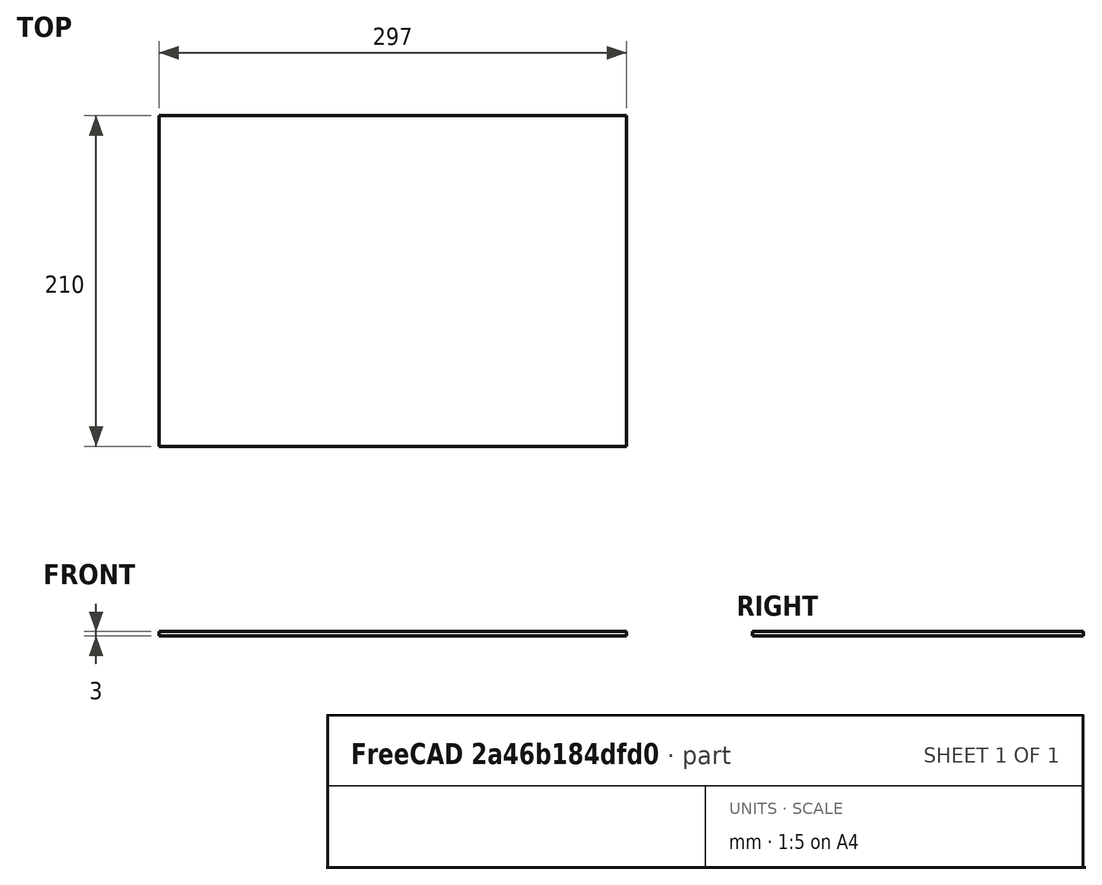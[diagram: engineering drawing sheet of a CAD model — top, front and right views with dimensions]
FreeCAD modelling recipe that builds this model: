
FCSTD DOCUMENT  (FreeCAD 0.20R29177 (Git))
Label: 1001_keyboard_Analog_paper_stencil_A4
License: All rights reserved
LicenseURL: http://en.wikipedia.org/wiki/All_rights_reserved
objects: Sketcher::SketchObject×6, PartDesign::Pad×1, PartDesign::Body×1
note: 9 computed .brp shape members not serialized (recipe doc carries the construction recipe); baked Part::Feature solids carry a one-line shape summary decoded from their .brp

FEATURE [Sketcher::SketchObject] Sketch
  FullyConstrained = true
  MapMode = 5
  Support = -> [XY_Plane]
  sketch-geometry (5):
    g0: LineSegment StartX=0 StartY=210 StartZ=0 EndX=297 EndY=210 EndZ=0
    g1: LineSegment StartX=297 StartY=210 StartZ=0 EndX=297 EndY=0 EndZ=0
    g2: LineSegment StartX=297 StartY=0 StartZ=0 EndX=0 EndY=0 EndZ=0
    g3: LineSegment StartX=0 StartY=0 StartZ=0 EndX=0 EndY=105 EndZ=0
    g4: LineSegment StartX=0 StartY=105 StartZ=0 EndX=0 EndY=210 EndZ=0
  constraints (14):
    c: Coincident(g0,g1)
    c: Coincident(g1,g2)
    c: Horizontal(g0)
    c: Horizontal(g2)
    c: Vertical(g1)
    c: DistanceY(g1,g1) = 210
    c: DistanceX(g0,g0) = 297
    c: Coincident(g3,g2)
    c: Coincident(g4,g0)
    c: Equal(g3,g4)
    c: Vertical(g4)
    c: Vertical(g3)
    c: Coincident(g3,g4)
    c: Coincident(g2,g-1)
FEATURE [PartDesign::Pad] Pad  label="A4_Landscape"
  AllowMultiFace = false
  Direction = (0,0,1)
  Length = 3
  Length2 = 100
  Profile = -> Sketch
  ReferenceAxis = -> Sketch [N_Axis]
  Type = 0
FEATURE [PartDesign::Body] Body
  Group = -> [Sketch,Pad]
  Origin = -> Origin
  Tip = -> Pad
FEATURE [Sketcher::SketchObject] Sketch002  label="ButtonsLayoutSquare"
  FullyConstrained = false
  sketch-geometry (15):
    g0: LineSegment StartX=130.72 StartY=61.5386 StartZ=0 EndX=130.72 EndY=21.5386 EndZ=0
    g1: Circle CenterX=130.72 CenterY=61.5386 CenterZ=0 NormalX=0 NormalY=0 NormalZ=1 AngleXU=0 Radius=15
    g2: Circle CenterX=130.72 CenterY=21.5386 CenterZ=0 NormalX=0 NormalY=0 NormalZ=1 AngleXU=0 Radius=15
    g3: LineSegment StartX=130.72 StartY=61.5386 StartZ=0 EndX=170.72 EndY=61.5386 EndZ=0
    g4: LineSegment StartX=130.72 StartY=21.5386 StartZ=0 EndX=170.72 EndY=21.5386 EndZ=0
    g5: LineSegment StartX=170.72 StartY=21.5386 StartZ=0 EndX=170.72 EndY=61.5386 EndZ=0
    g6: Circle CenterX=170.72 CenterY=61.5386 CenterZ=0 NormalX=0 NormalY=0 NormalZ=1 AngleXU=0 Radius=14.5
    g7: Circle CenterX=170.72 CenterY=21.5386 CenterZ=0 NormalX=0 NormalY=0 NormalZ=1 AngleXU=0 Radius=15
    g8: LineSegment StartX=130.72 StartY=21.5386 StartZ=0 EndX=150.72 EndY=41.5386 EndZ=0
    g9: LineSegment StartX=150.72 StartY=41.5386 StartZ=0 EndX=170.72 EndY=61.5386 EndZ=0
    g10: LineSegment StartX=110.72 StartY=81.5386 StartZ=0 EndX=110.72 EndY=1.53857 EndZ=0
    g11: LineSegment StartX=110.72 StartY=1.53857 StartZ=0 EndX=190.72 EndY=1.53857 EndZ=0
    g12: LineSegment StartX=190.72 StartY=1.53857 StartZ=0 EndX=190.72 EndY=81.5386 EndZ=0
    g13: LineSegment StartX=190.72 StartY=81.5386 StartZ=0 EndX=110.72 EndY=81.5386 EndZ=0
    g14: Circle CenterX=150.72 CenterY=41.5386 CenterZ=0 NormalX=0 NormalY=0 NormalZ=1 AngleXU=0 Radius=56.5685
  constraints (35):
    c: Equal(g2,g1)
    c: Coincident(g3,g1)
    c: Coincident(g4,g2)
    c: Coincident(g5,g4)
    c: Coincident(g5,g3)
    c: Equal(g3,g5)
    c: Equal(g5,g4)
    c: Coincident(g6,g3)
    c: Coincident(g7,g4)
    c: Coincident(g1,g0)
    c: Coincident(g0,g2)
    c: Angle(g0,g3) = 1.5708
    c: Distance(g6,g1) = 40
    c: Diameter(g6) = 29
    c: Vertical(g5)
    c: Vertical(g0)
    c: Coincident(g8,g2)
    c: Coincident(g9,g8)
    c: Coincident(g9,g6)
    c: Equal(g9,g8)
    c: Parallel(g9,g8)
    c: Coincident(g10,g11)
    c: Coincident(g11,g12)
    c: Coincident(g12,g13)
    c: Coincident(g13,g10)
    c: Equal(g10,g11)
    c: Equal(g10,g12)
    c: Equal(g10,g13)
    c: PointOnObject(g10,g14)
    c: PointOnObject(g11,g14)
    c: PointOnObject(g12,g14)
    c: PointOnObject(g13,g14)
    c: Coincident(g14,g8)
    c: Horizontal(g13)
    c: DistanceX(g13,g13) = 80
FEATURE [Sketcher::SketchObject] Sketch003  label="JoystickLayout4Way"
  FullyConstrained = false
  sketch-geometry (39):
    g0: LineSegment StartX=5 StartY=60 StartZ=0 EndX=100 EndY=60 EndZ=0
    g1: LineSegment StartX=100 StartY=60 StartZ=0 EndX=100 EndY=5 EndZ=0
    g2: LineSegment StartX=100 StartY=5 StartZ=0 EndX=52.5 EndY=5 EndZ=0
    g3: LineSegment StartX=52.5 StartY=5 StartZ=0 EndX=5 EndY=5 EndZ=0
    g4: LineSegment StartX=5 StartY=5 StartZ=0 EndX=5 EndY=32.5 EndZ=0
    g5: LineSegment StartX=5 StartY=32.5 StartZ=0 EndX=5 EndY=60 EndZ=0
    g6: LineSegment StartX=5 StartY=32.5 StartZ=0 EndX=52.5 EndY=32.5 EndZ=0
    g7: Circle CenterX=52.5 CenterY=32.5 CenterZ=0 NormalX=0 NormalY=0 NormalZ=1 AngleXU=0 Radius=15
    g8: LineSegment StartX=52.5 StartY=32.5 StartZ=0 EndX=100 EndY=32.5 EndZ=0
    g9: ArcOfCircle CenterX=10.5 CenterY=52.5 CenterZ=0 NormalX=0 NormalY=0 NormalZ=1 AngleXU=0 Radius=2.6 StartAngle=1.5708 EndAngle=4.71239
    g10: ArcOfCircle CenterX=13.1 CenterY=52.5 CenterZ=0 NormalX=0 NormalY=0 NormalZ=1 AngleXU=0 Radius=2.6 StartAngle=4.71239 EndAngle=7.85398
    g11: LineSegment StartX=10.5 StartY=49.9 StartZ=0 EndX=13.1 EndY=49.9 EndZ=0
    g12: LineSegment StartX=13.1 StartY=55.1 StartZ=0 EndX=10.5 EndY=55.1 EndZ=0
    g13: LineSegment StartX=10.5 StartY=55.1 StartZ=0 EndX=7.9 EndY=55.1 EndZ=0
    g14: LineSegment StartX=13.1 StartY=55.1 StartZ=0 EndX=15.7 EndY=55.1 EndZ=0
    g15: ArcOfCircle CenterX=94.5 CenterY=52.5 CenterZ=0 NormalX=0 NormalY=0 NormalZ=1 AngleXU=0 Radius=2.6 StartAngle=4.71239 EndAngle=7.85398
    g16: LineSegment StartX=94.5 StartY=55.1 StartZ=0 EndX=91.9 EndY=55.1 EndZ=0
    g17: LineSegment StartX=91.9 StartY=49.9 StartZ=0 EndX=94.5 EndY=49.9 EndZ=0
    g18: ArcOfCircle CenterX=91.9 CenterY=52.5 CenterZ=0 NormalX=0 NormalY=0 NormalZ=1 AngleXU=0 Radius=2.6 StartAngle=1.5708 EndAngle=4.71239
    g19: LineSegment StartX=10.5 StartY=9.9 StartZ=0 EndX=13.1 EndY=9.9 EndZ=0
    g20: ArcOfCircle CenterX=13.1 CenterY=12.5 CenterZ=0 NormalX=0 NormalY=0 NormalZ=1 AngleXU=0 Radius=2.6 StartAngle=4.71239 EndAngle=7.85398
    g21: LineSegment StartX=13.1 StartY=15.1 StartZ=0 EndX=10.5 EndY=15.1 EndZ=0
    g22: ArcOfCircle CenterX=10.5 CenterY=12.5 CenterZ=0 NormalX=0 NormalY=0 NormalZ=1 AngleXU=0 Radius=2.6 StartAngle=1.5708 EndAngle=4.71239
    g23: ArcOfCircle CenterX=91.9 CenterY=12.5 CenterZ=0 NormalX=0 NormalY=0 NormalZ=1 AngleXU=0 Radius=2.6 StartAngle=1.5708 EndAngle=4.71239
    g24: LineSegment StartX=91.9 StartY=9.9 StartZ=0 EndX=94.5 EndY=9.9 EndZ=0
    g25: LineSegment StartX=94.5 StartY=15.1 StartZ=0 EndX=91.9 EndY=15.1 EndZ=0
    g26: ArcOfCircle CenterX=94.5 CenterY=12.5 CenterZ=0 NormalX=0 NormalY=0 NormalZ=1 AngleXU=0 Radius=2.6 StartAngle=4.71239 EndAngle=7.85398
    g27: LineSegment StartX=52.5 StartY=5 StartZ=0 EndX=52.5 EndY=7.9007 EndZ=0
    g28: LineSegment StartX=5 StartY=32.5 StartZ=0 EndX=7.9007 EndY=32.5 EndZ=0
    g29: LineSegment StartX=100 StartY=32.5 StartZ=0 EndX=97.0993 EndY=32.5 EndZ=0
    g30: LineSegment StartX=52.5 StartY=60 StartZ=0 EndX=52.5 EndY=57.0993 EndZ=0
    g31: LineSegment StartX=100 StartY=60 StartZ=0 EndX=43 EndY=60 EndZ=0
    g32: LineSegment StartX=43 StartY=60 StartZ=0 EndX=43 EndY=70 EndZ=0
    g33: LineSegment StartX=23 StartY=70 StartZ=0 EndX=23 EndY=60 EndZ=0
    g34: LineSegment StartX=23 StartY=60 StartZ=0 EndX=5 EndY=60 EndZ=0
    g35: LineSegment StartX=23 StartY=70 StartZ=0 EndX=33 EndY=70 EndZ=0
    g36: LineSegment StartX=33 StartY=70 StartZ=0 EndX=43 EndY=70 EndZ=0
    g37: LineSegment StartX=10.5 StartY=49.9 StartZ=0 EndX=10.5 EndY=32.5 EndZ=0
    g38: LineSegment StartX=10.5 StartY=32.5 StartZ=0 EndX=10.5 EndY=15.1 EndZ=0
  constraints (107):
    c: Coincident(g0,g1)
    c: Coincident(g1,g2)
    c: Horizontal(g0)
    c: Horizontal(g2)
    c: Vertical(g1)
    c: DistanceY(g1,g1) = 55
    c: DistanceX(g0,g0) = 95
    c: Coincident(g3,g2)
    c: Coincident(g4,g3)
    c: Coincident(g5,g4)
    c: Coincident(g5,g0)
    c: Vertical(g5)
    c: Vertical(g4)
    c: Horizontal(g3)
    c: Equal(g3,g2)
    c: Equal(g4,g5)
    c: Coincident(g6,g4)
    c: Horizontal(g6)
    c: Coincident(g7,g6)
    c: Coincident(g8,g6)
    c: PointOnObject(g8,g1)
    c: Horizontal(g8)
    c: Equal(g8,g6)
    c: Diameter(g7) = 30
    c: Tangent(g9,g11) = -1.5708
    c: Tangent(g11,g10) = -1.5708
    c: Tangent(g10,g12) = -1.5708
    c: Tangent(g12,g9) = -1.5708
    c: Equal(g9,g10)
    c: Horizontal(g11)
    c: DistanceY(g10,g10) = 5.2
    c: Coincident(g13,g9)
    c: Horizontal(g13)
    c: Coincident(g14,g10)
    c: Horizontal(g14)
    c: Equal(g14,g13)
    c: DistanceX(g13,g13) = 2.6
    c: DistanceX(g13,g14) = 7.8
    c: Tangent(g18,g17) = -1.5708
    c: Tangent(g17,g15) = -1.5708
    c: Tangent(g15,g16) = -1.5708
    c: Tangent(g16,g18) = -1.5708
    c: Equal(g18,g15)
    c: Horizontal(g17)
    c: Equal(g10,g15) = 5.2
    c: Tangent(g22,g19) = -1.5708
    c: Tangent(g19,g20) = -1.5708
    c: Tangent(g20,g21) = -1.5708
    c: Tangent(g21,g22) = -1.5708
    c: Equal(g22,g20)
    c: Horizontal(g19)
    c: Equal(g10,g20) = 5.2
    c: Tangent(g23,g24) = -1.5708
    c: Tangent(g24,g26) = -1.5708
    c: Tangent(g26,g25) = -1.5708
    c: Tangent(g25,g23) = -1.5708
    c: Equal(g23,g26)
    c: Horizontal(g24)
    c: Equal(g10,g26) = 5.2
    c: Equal(g21,g16)
    c: Equal(g16,g25)
    c: Equal(g25,g11)
    c: Vertical(g21,g9)
    c: DistanceX(g9,g6) = 42
    c: Horizontal(g23,g20)
    c: Vertical(g23,g17)
    c: DistanceX(g9,g15) = 84
    c: Horizontal(g10,g16)
    c: Coincident(g27,g2)
    c: Vertical(g27)
    c: Coincident(g28,g4)
    c: PointOnObject(g28,g6)
    c: Equal(g28,g27)
    c: Coincident(g29,g8)
    c: PointOnObject(g29,g8)
    c: Equal(g29,g27)
    c: PointOnObject(g30,g0)
    c: Vertical(g30)
    c: Equal(g30,g29)
    c: Vertical(g30,g27)
    c: Coincident(g31,g1)
    c: PointOnObject(g31,g0)
    c: Coincident(g32,g31)
    c: Vertical(g32)
    c: PointOnObject(g33,g0)
    c: Vertical(g33)
    c: Coincident(g34,g33)
    c: Coincident(g34,g5)
    c: DistanceX(g33,g32) = 20
    c: DistanceY(g33,g33) = 10
    c: Coincident(g35,g33)
    c: Horizontal(g35)
    c: Coincident(g36,g35)
    c: Coincident(g36,g32)
    c: Horizontal(g36)
    c: Equal(g36,g35)
    c: DistanceX(g5,g35) = 28
    c: Coincident(g37,g9)
    c: PointOnObject(g37,g6)
    c: Vertical(g37)
    c: Coincident(g38,g37)
    c: Coincident(g38,g21)
    c: Equal(g38,g37)
    c: DistanceY(g22,g9) = 40
    c: DistanceX(g-1,g3) = 5
    c: DistanceY(g-1,g3) = 5
    c: DistanceX(g7,g15) = 42
FEATURE [Sketcher::SketchObject] Sketch007  label="JoystickAnalog"
  FullyConstrained = false
  MapMode = 5
  Support = -> [XY_Plane]
  sketch-geometry (90):
    g0: Circle CenterX=243.856 CenterY=93.0122 CenterZ=0 NormalX=0 NormalY=0 NormalZ=1 AngleXU=0 Radius=20
    g1: LineSegment StartX=243.856 StartY=93.0122 StartZ=0 EndX=201.356 EndY=93.0122 EndZ=0
    g2: LineSegment StartX=243.856 StartY=93.0122 StartZ=0 EndX=286.356 EndY=93.0122 EndZ=0
    g3: LineSegment StartX=201.356 StartY=93.0122 StartZ=0 EndX=201.356 EndY=113.012 EndZ=0
    g4: LineSegment StartX=201.356 StartY=93.0122 StartZ=0 EndX=201.356 EndY=73.0122 EndZ=0
    g5: LineSegment StartX=286.356 StartY=93.0122 StartZ=0 EndX=286.356 EndY=73.0122 EndZ=0
    g6: LineSegment StartX=286.356 StartY=93.0122 StartZ=0 EndX=286.356 EndY=113.012 EndZ=0
    g7: LineSegment StartX=243.856 StartY=93.0122 StartZ=0 EndX=243.856 EndY=123.012 EndZ=0
    g8: LineSegment StartX=243.856 StartY=93.0122 StartZ=0 EndX=243.856 EndY=63.0122 EndZ=0
    g9: LineSegment StartX=243.856 StartY=123.012 StartZ=0 EndX=196.356 EndY=123.012 EndZ=0
    g10: LineSegment StartX=243.856 StartY=123.012 StartZ=0 EndX=291.356 EndY=123.012 EndZ=0
    g11: LineSegment StartX=243.856 StartY=63.0122 StartZ=0 EndX=196.356 EndY=63.0122 EndZ=0
    g12: LineSegment StartX=196.356 StartY=63.0122 StartZ=0 EndX=196.356 EndY=123.012 EndZ=0
    g13: LineSegment StartX=243.856 StartY=63.0122 StartZ=0 EndX=291.356 EndY=63.0122 EndZ=0
    g14: LineSegment StartX=291.356 StartY=63.0122 StartZ=0 EndX=291.356 EndY=123.012 EndZ=0
    g15: ArcOfCircle CenterX=201.356 CenterY=113.012 CenterZ=0 NormalX=0 NormalY=0 NormalZ=1 AngleXU=0 Radius=2.5 StartAngle=1.5708 EndAngle=4.71239
    g16: ArcOfCircle CenterX=206.356 CenterY=113.012 CenterZ=0 NormalX=0 NormalY=0 NormalZ=1 AngleXU=0 Radius=2.5 StartAngle=4.71239 EndAngle=7.85398
    g17: LineSegment StartX=201.356 StartY=110.512 StartZ=0 EndX=206.356 EndY=110.512 EndZ=0
    g18: LineSegment StartX=206.356 StartY=115.512 StartZ=0 EndX=201.356 EndY=115.512 EndZ=0
    g19: ArcOfCircle CenterX=201.356 CenterY=73.0122 CenterZ=0 NormalX=0 NormalY=0 NormalZ=1 AngleXU=0 Radius=2.5 StartAngle=1.5708 EndAngle=4.71239
    g20: ArcOfCircle CenterX=206.356 CenterY=73.0122 CenterZ=0 NormalX=0 NormalY=0 NormalZ=1 AngleXU=0 Radius=2.5 StartAngle=4.71239 EndAngle=7.85398
    g21: LineSegment StartX=201.356 StartY=70.5122 StartZ=0 EndX=206.356 EndY=70.5122 EndZ=0
    g22: LineSegment StartX=206.356 StartY=75.5122 StartZ=0 EndX=201.356 EndY=75.5122 EndZ=0
    g23: ArcOfCircle CenterX=286.356 CenterY=73.0122 CenterZ=0 NormalX=0 NormalY=0 NormalZ=1 AngleXU=0 Radius=2.5 StartAngle=4.71239 EndAngle=7.85398
    g24: ArcOfCircle CenterX=281.356 CenterY=73.0122 CenterZ=0 NormalX=0 NormalY=0 NormalZ=1 AngleXU=0 Radius=2.5 StartAngle=1.5708 EndAngle=4.71239
    g25: LineSegment StartX=286.356 StartY=75.5122 StartZ=0 EndX=281.356 EndY=75.5122 EndZ=0
    g26: LineSegment StartX=281.356 StartY=70.5122 StartZ=0 EndX=286.356 EndY=70.5122 EndZ=0
    g27: ArcOfCircle CenterX=286.356 CenterY=113.012 CenterZ=0 NormalX=0 NormalY=0 NormalZ=1 AngleXU=0 Radius=2.5 StartAngle=4.71239 EndAngle=7.85398
    g28: ArcOfCircle CenterX=281.356 CenterY=113.012 CenterZ=0 NormalX=0 NormalY=0 NormalZ=1 AngleXU=0 Radius=2.5 StartAngle=1.5708 EndAngle=4.71239
    g29: LineSegment StartX=286.356 StartY=115.512 StartZ=0 EndX=281.356 EndY=115.512 EndZ=0
    g30: LineSegment StartX=281.356 StartY=110.512 StartZ=0 EndX=286.356 EndY=110.512 EndZ=0
    g31: LineSegment StartX=201.356 StartY=93.0122 StartZ=0 EndX=196.356 EndY=93.0122 EndZ=0
    g32: LineSegment StartX=286.356 StartY=93.0122 StartZ=0 EndX=291.356 EndY=93.0122 EndZ=0
    g33: LineSegment StartX=243.856 StartY=123.012 StartZ=0 EndX=243.856 EndY=118.012 EndZ=0
    g34: LineSegment StartX=196.356 StartY=63.0122 StartZ=0 EndX=236.356 EndY=63.0122 EndZ=0
    g35: LineSegment StartX=236.356 StartY=63.0122 StartZ=0 EndX=236.356 EndY=51.0122 EndZ=0
    g36: LineSegment StartX=236.356 StartY=51.0122 StartZ=0 EndX=251.356 EndY=51.0122 EndZ=0
    g37: LineSegment StartX=251.356 StartY=51.0122 StartZ=0 EndX=251.356 EndY=63.0122 EndZ=0
    g38: LineSegment StartX=251.356 StartY=63.0122 StartZ=0 EndX=291.356 EndY=63.0122 EndZ=0
    g39: LineSegment StartX=196.356 StartY=123.012 StartZ=0 EndX=228.856 EndY=123.012 EndZ=0
    g40: LineSegment StartX=228.856 StartY=123.012 StartZ=0 EndX=228.856 EndY=127.012 EndZ=0
    g41: LineSegment StartX=233.856 StartY=127.012 StartZ=0 EndX=233.856 EndY=123.012 EndZ=0
    g42: LineSegment StartX=233.856 StartY=123.012 StartZ=0 EndX=243.856 EndY=123.012 EndZ=0
    g43: LineSegment StartX=228.856 StartY=127.012 StartZ=0 EndX=231.356 EndY=127.012 EndZ=0
    g44: LineSegment StartX=231.356 StartY=127.012 StartZ=0 EndX=233.856 EndY=127.012 EndZ=0
    g45: Circle CenterX=242.711 CenterY=174.033 CenterZ=0 NormalX=0 NormalY=0 NormalZ=1 AngleXU=0 Radius=20
    g46: LineSegment StartX=242.711 StartY=174.033 StartZ=0 EndX=200.211 EndY=174.033 EndZ=0
    g47: LineSegment StartX=242.711 StartY=174.033 StartZ=0 EndX=285.211 EndY=174.033 EndZ=0
    g48: LineSegment StartX=200.211 StartY=174.033 StartZ=0 EndX=200.211 EndY=194.033 EndZ=0
    g49: LineSegment StartX=200.211 StartY=174.033 StartZ=0 EndX=200.211 EndY=154.033 EndZ=0
    g50: LineSegment StartX=285.211 StartY=174.033 StartZ=0 EndX=285.211 EndY=154.033 EndZ=0
    g51: LineSegment StartX=285.211 StartY=174.033 StartZ=0 EndX=285.211 EndY=194.033 EndZ=0
    g52: LineSegment StartX=242.711 StartY=174.033 StartZ=0 EndX=242.711 EndY=204.033 EndZ=0
    g53: LineSegment StartX=242.711 StartY=174.033 StartZ=0 EndX=242.711 EndY=144.033 EndZ=0
    g54: LineSegment StartX=242.711 StartY=204.033 StartZ=0 EndX=195.211 EndY=204.033 EndZ=0
    g55: LineSegment StartX=242.711 StartY=204.033 StartZ=0 EndX=290.211 EndY=204.033 EndZ=0
    g56: LineSegment StartX=242.711 StartY=144.033 StartZ=0 EndX=195.211 EndY=144.033 EndZ=0
    g57: LineSegment StartX=195.211 StartY=144.033 StartZ=0 EndX=195.211 EndY=204.033 EndZ=0
    g58: LineSegment StartX=242.711 StartY=144.033 StartZ=0 EndX=290.211 EndY=144.033 EndZ=0
    g59: LineSegment StartX=290.211 StartY=144.033 StartZ=0 EndX=290.211 EndY=204.033 EndZ=0
    g60: ArcOfCircle CenterX=200.211 CenterY=194.033 CenterZ=0 NormalX=0 NormalY=0 NormalZ=1 AngleXU=0 Radius=2.5 StartAngle=1.5708 EndAngle=4.71239
    g61: ArcOfCircle CenterX=205.211 CenterY=194.033 CenterZ=0 NormalX=0 NormalY=0 NormalZ=1 AngleXU=0 Radius=2.5 StartAngle=4.71239 EndAngle=7.85398
    g62: LineSegment StartX=200.211 StartY=191.533 StartZ=0 EndX=205.211 EndY=191.533 EndZ=0
    g63: LineSegment StartX=205.211 StartY=196.533 StartZ=0 EndX=200.211 EndY=196.533 EndZ=0
    g64: ArcOfCircle CenterX=200.211 CenterY=154.033 CenterZ=0 NormalX=0 NormalY=0 NormalZ=1 AngleXU=0 Radius=2.5 StartAngle=1.5708 EndAngle=4.71239
    g65: ArcOfCircle CenterX=205.211 CenterY=154.033 CenterZ=0 NormalX=0 NormalY=0 NormalZ=1 AngleXU=0 Radius=2.5 StartAngle=4.71239 EndAngle=7.85398
    g66: LineSegment StartX=200.211 StartY=151.533 StartZ=0 EndX=205.211 EndY=151.533 EndZ=0
    g67: LineSegment StartX=205.211 StartY=156.533 StartZ=0 EndX=200.211 EndY=156.533 EndZ=0
    g68: ArcOfCircle CenterX=285.211 CenterY=154.033 CenterZ=0 NormalX=0 NormalY=0 NormalZ=1 AngleXU=0 Radius=2.5 StartAngle=4.71239 EndAngle=7.85398
    g69: ArcOfCircle CenterX=280.211 CenterY=154.033 CenterZ=0 NormalX=0 NormalY=0 NormalZ=1 AngleXU=0 Radius=2.5 StartAngle=1.5708 EndAngle=4.71239
    g70: LineSegment StartX=285.211 StartY=156.533 StartZ=0 EndX=280.211 EndY=156.533 EndZ=0
    g71: LineSegment StartX=280.211 StartY=151.533 StartZ=0 EndX=285.211 EndY=151.533 EndZ=0
    g72: ArcOfCircle CenterX=285.211 CenterY=194.033 CenterZ=0 NormalX=0 NormalY=0 NormalZ=1 AngleXU=0 Radius=2.5 StartAngle=4.71239 EndAngle=7.85398
    g73: ArcOfCircle CenterX=280.211 CenterY=194.033 CenterZ=0 NormalX=0 NormalY=0 NormalZ=1 AngleXU=0 Radius=2.5 StartAngle=1.5708 EndAngle=4.71239
    g74: LineSegment StartX=285.211 StartY=196.533 StartZ=0 EndX=280.211 EndY=196.533 EndZ=0
    g75: LineSegment StartX=280.211 StartY=191.533 StartZ=0 EndX=285.211 EndY=191.533 EndZ=0
    g76: LineSegment StartX=200.211 StartY=174.033 StartZ=0 EndX=195.211 EndY=174.033 EndZ=0
    g77: LineSegment StartX=285.211 StartY=174.033 StartZ=0 EndX=290.211 EndY=174.033 EndZ=0
    g78: LineSegment StartX=242.711 StartY=204.033 StartZ=0 EndX=242.711 EndY=199.033 EndZ=0
    g79: LineSegment StartX=195.211 StartY=144.033 StartZ=0 EndX=235.211 EndY=144.033 EndZ=0
    g80: LineSegment StartX=235.211 StartY=144.033 StartZ=0 EndX=235.211 EndY=132.033 EndZ=0
    g81: LineSegment StartX=235.211 StartY=132.033 StartZ=0 EndX=250.211 EndY=132.033 EndZ=0
    g82: LineSegment StartX=250.211 StartY=132.033 StartZ=0 EndX=250.211 EndY=144.033 EndZ=0
    g83: LineSegment StartX=250.211 StartY=144.033 StartZ=0 EndX=290.211 EndY=144.033 EndZ=0
    g84: LineSegment StartX=195.211 StartY=204.033 StartZ=0 EndX=227.711 EndY=204.033 EndZ=0
    g85: LineSegment StartX=227.711 StartY=204.033 StartZ=0 EndX=227.711 EndY=208.033 EndZ=0
    g86: LineSegment StartX=232.711 StartY=208.033 StartZ=0 EndX=232.711 EndY=204.033 EndZ=0
    g87: LineSegment StartX=232.711 StartY=204.033 StartZ=0 EndX=242.711 EndY=204.033 EndZ=0
    g88: LineSegment StartX=227.711 StartY=208.033 StartZ=0 EndX=230.211 EndY=208.033 EndZ=0
    g89: LineSegment StartX=230.211 StartY=208.033 StartZ=0 EndX=232.711 EndY=208.033 EndZ=0
  constraints (234):
    c: Diameter(g0) = 40
    c: Coincident(g1,g0)
    c: Horizontal(g1)
    c: Coincident(g2,g0)
    c: Horizontal(g2)
    c: Coincident(g3,g1)
    c: Vertical(g3)
    c: Coincident(g4,g1)
    c: Vertical(g4)
    c: Coincident(g5,g2)
    c: Vertical(g5)
    c: Coincident(g6,g2)
    c: Vertical(g6)
    c: Equal(g4,g3)
    c: Equal(g3,g5)
    c: Equal(g5,g6)
    c: Equal(g2,g1)
    c: Coincident(g7,g0)
    c: Vertical(g7)
    c: Coincident(g8,g0)
    c: Vertical(g8)
    c: Equal(g8,g7)
    c: DistanceY(g4,g3) = 40
    c: DistanceX(g3,g6) = 85
    c: DistanceY(g8,g7) = 60
    c: Coincident(g9,g7)
    c: Coincident(g10,g9)
    c: Equal(g10,g9)
    c: Horizontal(g9)
    c: Horizontal(g10)
    c: DistanceX(g9,g10) = 95
    c: Coincident(g11,g8)
    c: Horizontal(g11)
    c: Coincident(g12,g9)
    c: Vertical(g12)
    c: Coincident(g13,g11)
    c: Coincident(g14,g13)
    c: Coincident(g14,g10)
    c: Horizontal(g13)
    c: Vertical(g14)
    c: Coincident(g11,g12)
    c: Tangent(g15,g17) = -1.5708
    c: Tangent(g17,g16) = -1.5708
    c: Tangent(g16,g18) = -1.5708
    c: Tangent(g18,g15) = -1.5708
    c: Equal(g15,g16)
    c: Coincident(g15,g3)
    c: Horizontal(g17)
    c: Tangent(g19,g21) = -1.5708
    c: Tangent(g21,g20) = -1.5708
    c: Tangent(g20,g22) = -1.5708
    c: Tangent(g22,g19) = -1.5708
    c: Equal(g19,g20)
    c: Coincident(g19,g4)
    c: Horizontal(g21)
    c: Tangent(g23,g25) = -1.5708
    c: Tangent(g25,g24) = -1.5708
    c: Tangent(g24,g26) = -1.5708
    c: Tangent(g26,g23) = -1.5708
    c: Equal(g23,g24)
    c: Coincident(g23,g5)
    c: Horizontal(g25)
    c: Tangent(g27,g29) = -1.5708
    c: Tangent(g29,g28) = -1.5708
    c: Tangent(g28,g30) = -1.5708
    c: Tangent(g30,g27) = -1.5708
    c: Equal(g27,g28)
    c: Coincident(g27,g6)
    c: Horizontal(g29)
    c: Equal(g18,g22)
    c: Equal(g22,g25)
    c: Equal(g25,g29)
    c: Equal(g20,g24)
    c: Equal(g24,g28)
    c: Equal(g28,g16)
    c: Diameter(g16) = 5
    c: DistanceX(g18,g18) = 5
    c: Coincident(g31,g1)
    c: PointOnObject(g31,g12)
    c: Horizontal(g31)
    c: Coincident(g32,g2)
    c: PointOnObject(g32,g14)
    c: Horizontal(g32)
    c: Coincident(g33,g9)
    c: PointOnObject(g33,g7)
    c: Equal(g33,g32)
    c: Coincident(g34,g12)
    c: PointOnObject(g34,g11)
    c: Coincident(g35,g34)
    c: Vertical(g35)
    c: Coincident(g36,g35)
    c: Horizontal(g36)
    c: Coincident(g37,g36)
    c: PointOnObject(g37,g13)
    c: Coincident(g38,g37)
    c: Coincident(g38,g14)
    c: Equal(g38,g34)
    c: DistanceX(g36,g36) = 15
    c: DistanceY(g35,g35) = 12
    c: Coincident(g39,g12)
    c: PointOnObject(g39,g9)
    c: Coincident(g40,g39)
    c: PointOnObject(g41,g9)
    c: Coincident(g42,g41)
    c: Coincident(g42,g10)
    c: Vertical(g40)
    c: Vertical(g41)
    c: Coincident(g43,g40)
    c: Horizontal(g43)
    c: Coincident(g44,g43)
    c: Coincident(g44,g41)
    c: Horizontal(g44)
    c: Equal(g44,g43)
    c: DistanceX(g12,g43) = 35
    c: DistanceX(g40,g41) = 5
    c: DistanceY(g40,g40) = 4
    c: Vertical(g37)
    c: Equal(g0,g45) = 40
    c: Coincident(g46,g45)
    c: Horizontal(g46)
    c: Coincident(g47,g45)
    c: Horizontal(g47)
    c: Coincident(g48,g46)
    c: Vertical(g48)
    c: Coincident(g49,g46)
    c: Vertical(g49)
    c: Coincident(g50,g47)
    c: Vertical(g50)
    c: Coincident(g51,g47)
    c: Vertical(g51)
    c: Equal(g49,g48)
    c: Equal(g48,g50)
    c: Equal(g50,g51)
    c: Equal(g47,g46)
    c: Coincident(g52,g45)
    c: Vertical(g52)
    c: Coincident(g53,g45)
    c: Vertical(g53)
    c: Equal(g53,g52)
    c: DistanceY(g49,g48) = 40
    c: DistanceX(g48,g51) = 85
    c: DistanceY(g53,g52) = 60
    c: Coincident(g54,g52)
    c: Coincident(g55,g54)
    c: Equal(g55,g54)
    c: Horizontal(g54)
    c: Horizontal(g55)
    c: DistanceX(g54,g55) = 95
    c: Coincident(g56,g53)
    c: Horizontal(g56)
    c: Coincident(g57,g54)
    c: Vertical(g57)
    c: Coincident(g58,g56)
    c: Coincident(g59,g58)
    c: Coincident(g59,g55)
    c: Horizontal(g58)
    c: Vertical(g59)
    c: Coincident(g56,g57)
    c: Tangent(g60,g62) = -1.5708
    c: Tangent(g62,g61) = -1.5708
    c: Tangent(g61,g63) = -1.5708
    c: Tangent(g63,g60) = -1.5708
    c: Equal(g60,g61)
    c: Coincident(g60,g48)
    c: Horizontal(g62)
    c: Tangent(g64,g66) = -1.5708
    c: Tangent(g66,g65) = -1.5708
    c: Tangent(g65,g67) = -1.5708
    c: Tangent(g67,g64) = -1.5708
    c: Equal(g64,g65)
    c: Coincident(g64,g49)
    c: Horizontal(g66)
    c: Tangent(g68,g70) = -1.5708
    c: Tangent(g70,g69) = -1.5708
    c: Tangent(g69,g71) = -1.5708
    c: Tangent(g71,g68) = -1.5708
    c: Equal(g68,g69)
    c: Coincident(g68,g50)
    c: Horizontal(g70)
    c: Tangent(g72,g74) = -1.5708
    c: Tangent(g74,g73) = -1.5708
    c: Tangent(g73,g75) = -1.5708
    c: Tangent(g75,g72) = -1.5708
    c: Equal(g72,g73)
    c: Coincident(g72,g51)
    c: Horizontal(g74)
    c: Equal(g63,g67)
    c: Equal(g67,g70)
    c: Equal(g70,g74)
    c: Equal(g65,g69)
    c: Equal(g69,g73)
    c: Equal(g73,g61)
    c: Equal(g16,g61) = 5
    c: Equal(g18,g63) = 5
    c: Coincident(g76,g46)
    c: PointOnObject(g76,g57)
    c: Horizontal(g76)
    c: Coincident(g77,g47)
    c: PointOnObject(g77,g59)
    c: Horizontal(g77)
    c: Coincident(g78,g54)
    c: PointOnObject(g78,g52)
    c: Equal(g78,g77)
    c: Coincident(g79,g57)
    c: PointOnObject(g79,g56)
    c: Coincident(g80,g79)
    c: Vertical(g80)
    c: Coincident(g81,g80)
    c: Horizontal(g81)
    c: Coincident(g82,g81)
    c: PointOnObject(g82,g58)
    c: Coincident(g83,g82)
    c: Coincident(g83,g59)
    c: Equal(g83,g79)
    c: Equal(g36,g81) = 15
    c: Equal(g35,g80) = 12
    c: Coincident(g84,g57)
    c: PointOnObject(g84,g54)
    c: Coincident(g85,g84)
    c: PointOnObject(g86,g54)
    c: Coincident(g87,g86)
    c: Coincident(g87,g55)
    c: Vertical(g85)
    c: Vertical(g86)
    c: Coincident(g88,g85)
    c: Horizontal(g88)
    c: Coincident(g89,g88)
    c: Coincident(g89,g86)
    c: Horizontal(g89)
    c: Equal(g89,g88)
    c: DistanceX(g57,g88) = 35
    c: DistanceX(g85,g86) = 5
    c: Equal(g40,g85) = 4
    c: Vertical(g82)
FEATURE [Sketcher::SketchObject] Sketch008  label="ButtonsLayoutLTLS"
  FullyConstrained = false
  sketch-geometry (20):
    g0: Circle CenterX=26.5961 CenterY=184.248 CenterZ=0 NormalX=0 NormalY=0 NormalZ=1 AngleXU=0 Radius=15
    g1: Circle CenterX=66.5961 CenterY=184.248 CenterZ=0 NormalX=0 NormalY=0 NormalZ=1 AngleXU=0 Radius=14.5
    g2: LineSegment StartX=86.5961 StartY=204.248 StartZ=0 EndX=6.59611 EndY=204.248 EndZ=0
    g3: LineSegment StartX=46.5961 StartY=164.248 StartZ=0 EndX=6.59611 EndY=164.248 EndZ=0
    g4: LineSegment StartX=46.5961 StartY=164.248 StartZ=0 EndX=86.5961 EndY=164.248 EndZ=0
    g5: LineSegment StartX=86.5961 StartY=204.248 StartZ=0 EndX=86.5961 EndY=164.248 EndZ=0
    g6: LineSegment StartX=6.59611 StartY=204.248 StartZ=0 EndX=6.59611 EndY=184.248 EndZ=0
    g7: LineSegment StartX=6.59611 StartY=184.248 StartZ=0 EndX=6.59611 EndY=164.248 EndZ=0
    g8: LineSegment StartX=26.5961 StartY=184.248 StartZ=0 EndX=46.5961 EndY=184.248 EndZ=0
    g9: LineSegment StartX=46.5961 StartY=184.248 StartZ=0 EndX=66.5961 EndY=184.248 EndZ=0
    g10: Circle CenterX=121.724 CenterY=184.216 CenterZ=0 NormalX=0 NormalY=0 NormalZ=1 AngleXU=0 Radius=15
    g11: Circle CenterX=161.724 CenterY=184.216 CenterZ=0 NormalX=0 NormalY=0 NormalZ=1 AngleXU=0 Radius=14.5
    g12: LineSegment StartX=181.724 StartY=204.216 StartZ=0 EndX=101.724 EndY=204.216 EndZ=0
    g13: LineSegment StartX=141.724 StartY=164.216 StartZ=0 EndX=101.724 EndY=164.216 EndZ=0
    g14: LineSegment StartX=141.724 StartY=164.216 StartZ=0 EndX=181.724 EndY=164.216 EndZ=0
    g15: LineSegment StartX=181.724 StartY=204.216 StartZ=0 EndX=181.724 EndY=164.216 EndZ=0
    g16: LineSegment StartX=101.724 StartY=204.216 StartZ=0 EndX=101.724 EndY=184.216 EndZ=0
    g17: LineSegment StartX=101.724 StartY=184.216 StartZ=0 EndX=101.724 EndY=164.216 EndZ=0
    g18: LineSegment StartX=121.724 StartY=184.216 StartZ=0 EndX=141.724 EndY=184.216 EndZ=0
    g19: LineSegment StartX=141.724 StartY=184.216 StartZ=0 EndX=161.724 EndY=184.216 EndZ=0
  constraints (52):
    c: Distance(g1,g0) = 40
    c: Diameter(g1) = 29
    c: Horizontal(g2)
    c: DistanceX(g2,g2) = 80
    c: Horizontal(g3)
    c: Coincident(g4,g3)
    c: Horizontal(g4)
    c: Coincident(g5,g2)
    c: Coincident(g5,g4)
    c: Vertical(g5)
    c: Coincident(g6,g2)
    c: Vertical(g6)
    c: Coincident(g7,g6)
    c: Coincident(g7,g3)
    c: Vertical(g7)
    c: Coincident(g8,g0)
    c: Horizontal(g8)
    c: Coincident(g9,g8)
    c: Coincident(g9,g1)
    c: Horizontal(g9)
    c: Horizontal(g0,g6)
    c: Vertical(g8,g3)
    c: Equal(g7,g6)
    c: Equal(g4,g3)
    c: Equal(g9,g8)
    c: DistanceY(g5,g5) = 40
    c: Distance(g11,g10) = 40
    c: Diameter(g11) = 29
    c: Horizontal(g12)
    c: DistanceX(g12,g12) = 80
    c: Horizontal(g13)
    c: Coincident(g14,g13)
    c: Horizontal(g14)
    c: Coincident(g15,g12)
    c: Coincident(g15,g14)
    c: Vertical(g15)
    c: Coincident(g16,g12)
    c: Vertical(g16)
    c: Coincident(g17,g16)
    c: Coincident(g17,g13)
    c: Vertical(g17)
    c: Coincident(g18,g10)
    c: Horizontal(g18)
    c: Coincident(g19,g18)
    c: Coincident(g19,g11)
    c: Horizontal(g19)
    c: Horizontal(g10,g16)
    c: Vertical(g18,g13)
    c: Equal(g17,g16)
    c: Equal(g14,g13)
    c: Equal(g19,g18)
    c: DistanceY(g15,g15) = 40
FEATURE [Sketcher::SketchObject] Sketch009  label="ButtonsLayoutSelHotStart"
  FullyConstrained = false
  sketch-geometry (12):
    g0: Circle CenterX=67.6301 CenterY=137.073 CenterZ=0 NormalX=0 NormalY=0 NormalZ=1 AngleXU=0 Radius=15
    g1: Circle CenterX=27.6301 CenterY=137.073 CenterZ=0 NormalX=0 NormalY=0 NormalZ=1 AngleXU=0 Radius=15
    g2: LineSegment StartX=67.6301 StartY=137.073 StartZ=0 EndX=107.63 EndY=137.073 EndZ=0
    g3: Circle CenterX=107.63 CenterY=137.073 CenterZ=0 NormalX=0 NormalY=0 NormalZ=1 AngleXU=0 Radius=14.5
    g4: LineSegment StartX=67.6301 StartY=137.073 StartZ=0 EndX=27.6301 EndY=137.073 EndZ=0
    g5: LineSegment StartX=67.6301 StartY=137.073 StartZ=0 EndX=67.6301 EndY=157.073 EndZ=0
    g6: LineSegment StartX=67.6301 StartY=157.073 StartZ=0 EndX=7.63005 EndY=157.073 EndZ=0
    g7: LineSegment StartX=7.63005 StartY=157.073 StartZ=0 EndX=7.63005 EndY=117.073 EndZ=0
    g8: LineSegment StartX=7.63005 StartY=117.073 StartZ=0 EndX=127.63 EndY=117.073 EndZ=0
    g9: LineSegment StartX=127.63 StartY=117.073 StartZ=0 EndX=127.63 EndY=137.073 EndZ=0
    g10: LineSegment StartX=127.63 StartY=137.073 StartZ=0 EndX=127.63 EndY=157.073 EndZ=0
    g11: LineSegment StartX=127.63 StartY=157.073 StartZ=0 EndX=67.6301 EndY=157.073 EndZ=0
  constraints (30):
    c: Equal(g1,g0)
    c: Coincident(g2,g0)
    c: Coincident(g3,g2)
    c: Distance(g3,g0) = 40
    c: Diameter(g3) = 29
    c: Coincident(g4,g0)
    c: Coincident(g4,g1)
    c: Equal(g4,g2)
    c: Horizontal(g4)
    c: Coincident(g5,g0)
    c: Vertical(g5)
    c: Coincident(g6,g5)
    c: Horizontal(g6)
    c: Coincident(g7,g6)
    c: Vertical(g7)
    c: Horizontal(g8)
    c: Coincident(g9,g8)
    c: Vertical(g9)
    c: Coincident(g10,g9)
    c: Vertical(g10)
    c: Coincident(g11,g10)
    c: Coincident(g11,g6)
    c: Horizontal(g11)
    c: Horizontal(g9,g3)
    c: Equal(g11,g6)
    c: Coincident(g8,g7)
    c: Equal(g9,g10)
    c: Horizontal(g2)
    c: DistanceY(g7,g7) = 40
    c: DistanceX(g6,g10) = 120
